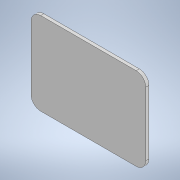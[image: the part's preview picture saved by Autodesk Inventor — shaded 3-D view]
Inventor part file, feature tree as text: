
AUTODESK INVENTOR PART (.ipt)
format: ipt  version: 2020 (Build 240168000, 168)  size: 98,304 bytes
history: native  units: mm
features: extrude x1, sketch x1
ambient origin geometry x8: Origin, YZ Plane, XZ Plane, XY Plane, X Axis, Y Axis, Z Axis, Center Point
bodies: Solid1 (feature_tree)
feature tree (2):
  extrude  "Extrusion1"  Depth=180.0mm
  sketch  "Sketch1"  dims[d0=130.0mm d1=180.0mm d2=15.0mm d3=15.0mm d4=5.0mm d5=0.0mm]
